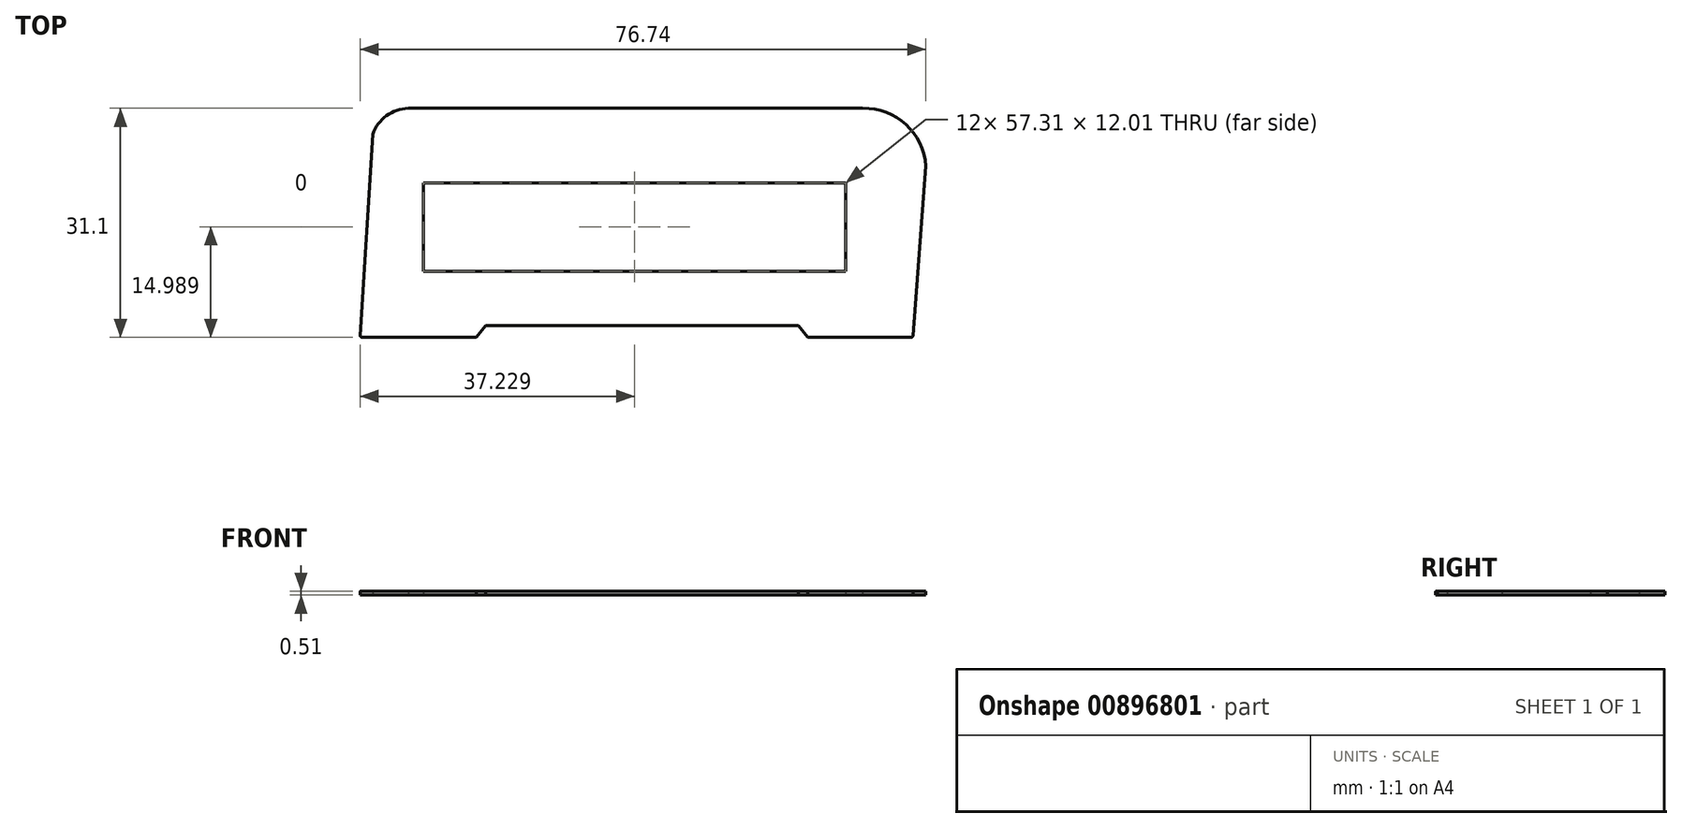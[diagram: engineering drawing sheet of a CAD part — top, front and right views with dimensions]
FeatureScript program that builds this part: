
annotation { "Feature Type Name" : "Feature", "Feature Type Description" : "" }
export const myFeature = defineFeature(function(context is Context, id is Id, definition is map)
    precondition{}
    {
        {
            var Q0;
            Q0=qCreatedBy(makeId("Top.planeOp"),FACE);
            var sketch = newSketch(context, id + "F0", { "sketchPlane" : qUnion([Q0])});
            skArc(sketch, "E0", {"start": v(-38.49, -15.28) * mm, "mid": v(-38.41, -15.47) * mm, "end": v(-38.23, -15.55) * mm});
            skLineSegment(sketch, "E1", {"start": v(-38.23, -15.55) * mm, "end": v(-22.75, -15.55) * mm});
            skLineSegment(sketch, "E2", {"start": v(-22.75, -15.55) * mm, "end": v(-21.48, -13.96) * mm});
            skLineSegment(sketch, "E3", {"start": v(-21.48, -13.96) * mm, "end": v(20.98, -13.96) * mm});
            skLineSegment(sketch, "E4", {"start": v(20.98, -13.96) * mm, "end": v(22.25, -15.55) * mm});
            skLineSegment(sketch, "E5", {"start": v(22.25, -15.55) * mm, "end": v(36.26, -15.55) * mm});
            skArc(sketch, "E6", {"start": v(36.26, -15.55) * mm, "mid": v(36.44, -15.47) * mm, "end": v(36.51, -15.3) * mm});
            skArc(sketch, "E7", {"start": v(38.25, 7.72) * mm, "mid": v(35.55, 13.36) * mm, "end": v(29.7, 15.54) * mm});
            skLineSegment(sketch, "E8", {"start": v(29.7, 15.54) * mm, "end": v(-31.94, 15.54) * mm});
            skArc(sketch, "E9", {"start": v(-31.94, 15.54) * mm, "mid": v(-34.9, 14.55) * mm, "end": v(-36.75, 12.04) * mm});
            skLineSegment(sketch, "E10", {"start": v(-36.75, 12.04) * mm, "end": v(-38.49, -15.28) * mm});
            skLineSegment(sketch, "E11", {"start": v(38.25, 7.72) * mm, "end": v(36.51, -15.3) * mm});
            skLineSegment(sketch, "E12.bottom", {"start": v(-29.92, 5.44) * mm, "end": v(27.4, 5.44) * mm});
            skLineSegment(sketch, "E12.top", {"start": v(-29.92, -6.56) * mm, "end": v(27.4, -6.56) * mm});
            skLineSegment(sketch, "E12.left", {"start": v(-29.92, 5.44) * mm, "end": v(-29.92, -6.56) * mm});
            skLineSegment(sketch, "E12.right", {"start": v(27.4, 5.44) * mm, "end": v(27.4, -6.56) * mm});
            skSolve(sketch);
        }
        {
            var Q0;
            Q0=makeQuery(id+"F0.imprint","IMPRINT",FACE,{"disambiguationData":[TD([[makeQuery(id+"F0.imprint","IMPRINT",EDGE,{"derivedFrom":sQuery(id+"F0.wireOp",EDGE,"E0")}),1.0]])]});
            extrude(context, id + "F1", {"entities" : qUnion([Q0]), "depth" : 0.5 * mm, "offsetDistance" : 25.4 * mm});
        }
    });
